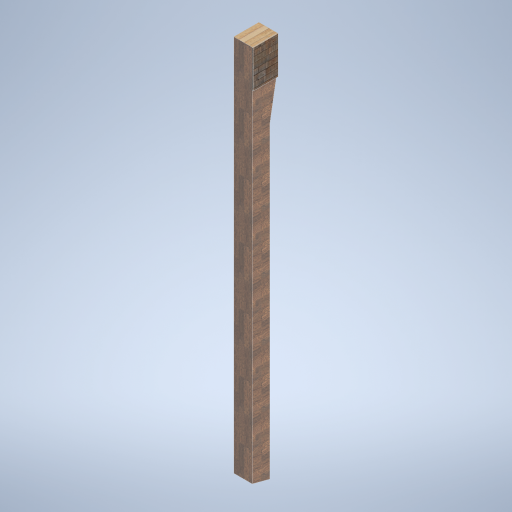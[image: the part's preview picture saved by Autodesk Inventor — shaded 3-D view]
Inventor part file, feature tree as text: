
AUTODESK INVENTOR PART (.ipt)
format: ipt  version: 2024.2 (Build 282272000, 272)  size: 338,432 bytes
history: native  units: mm
features: extrude x2, sketch x2
ambient origin geometry x8: Origin, YZ Plane, XZ Plane, XY Plane, X Axis, Y Axis, Z Axis, Center Point
bodies: Solid1 (feature_tree)
feature tree (4):
  extrude  "Extrusion1"  Depth=40000.000002mm
  extrude  "Extrusion2"  Depth=10.0mm
  sketch  "Sketch2"  dims[d0=40000.000002mm d1=300.0mm]
  sketch  "Sketch3"  dims[d2=200.0mm d3=0.0mm d5=400.0mm d6=1.745329mm d7=1.745329mm d8=10.0mm d9=10.0mm d10=10.0mm d11=0.0mm d12=500.0mm d13=0.872665mm d14=500.0mm d15=0.872665mm]
